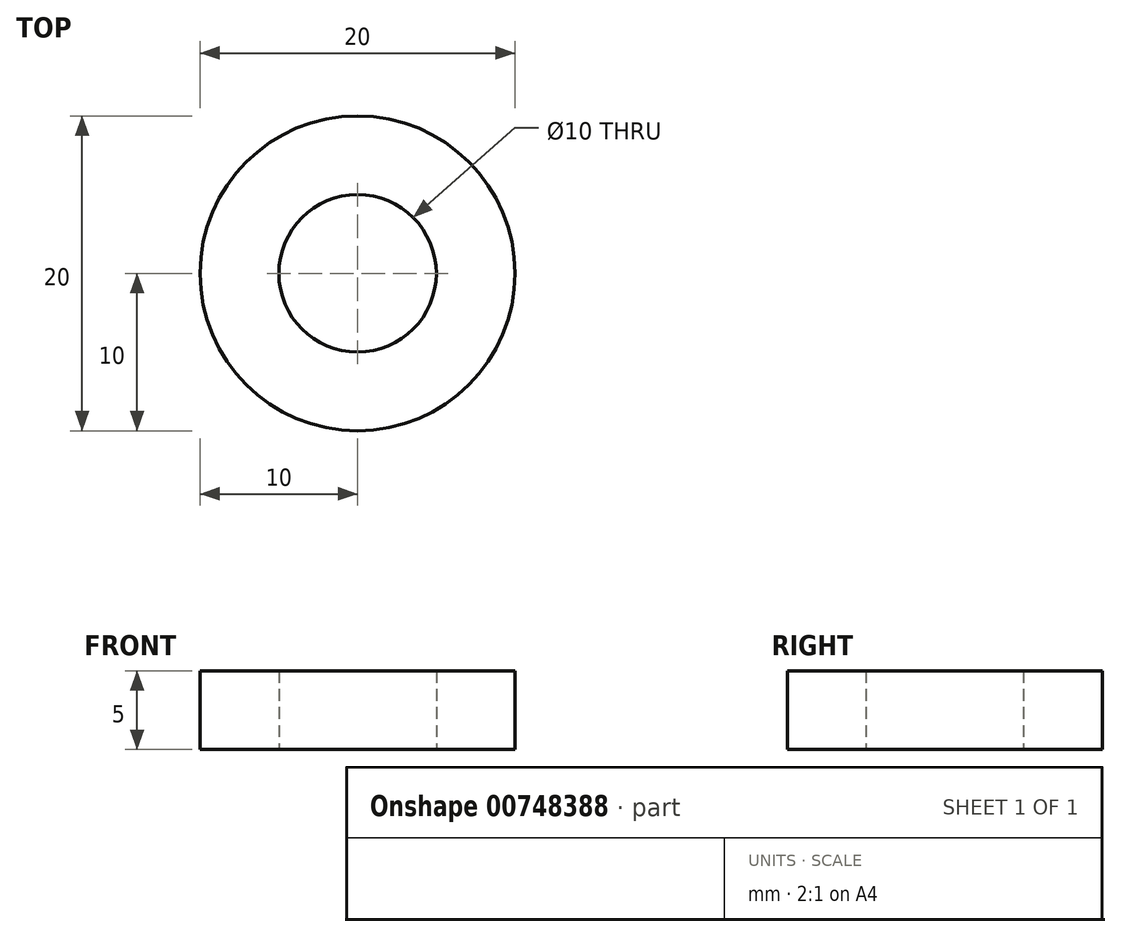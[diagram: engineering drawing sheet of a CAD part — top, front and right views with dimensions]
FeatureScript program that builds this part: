
annotation { "Feature Type Name" : "Feature", "Feature Type Description" : "" }
export const myFeature = defineFeature(function(context is Context, id is Id, definition is map)
    precondition{}
    {
        {
            var Q0;
            Q0=qCreatedBy(makeId("Top.planeOp"),FACE);
            var sketch = newSketch(context, id + "F0", { "sketchPlane" : qUnion([Q0])});
            skCircle(sketch, "E0", {"center": v(0, 0) * mm, "radius": 10 * mm});
            skCircle(sketch, "E1", {"center": v(0, 0) * mm, "radius": 5 * mm});
            skSolve(sketch);
        }
        {
            var Q0;
            Q0 = qSketchRegion(id + "F0", true);
            extrude(context, id + "F1", {"entities" : qUnion([Q0]), "depth" : 5 * mm, "offsetDistance" : 25 * mm});
        }
    });
